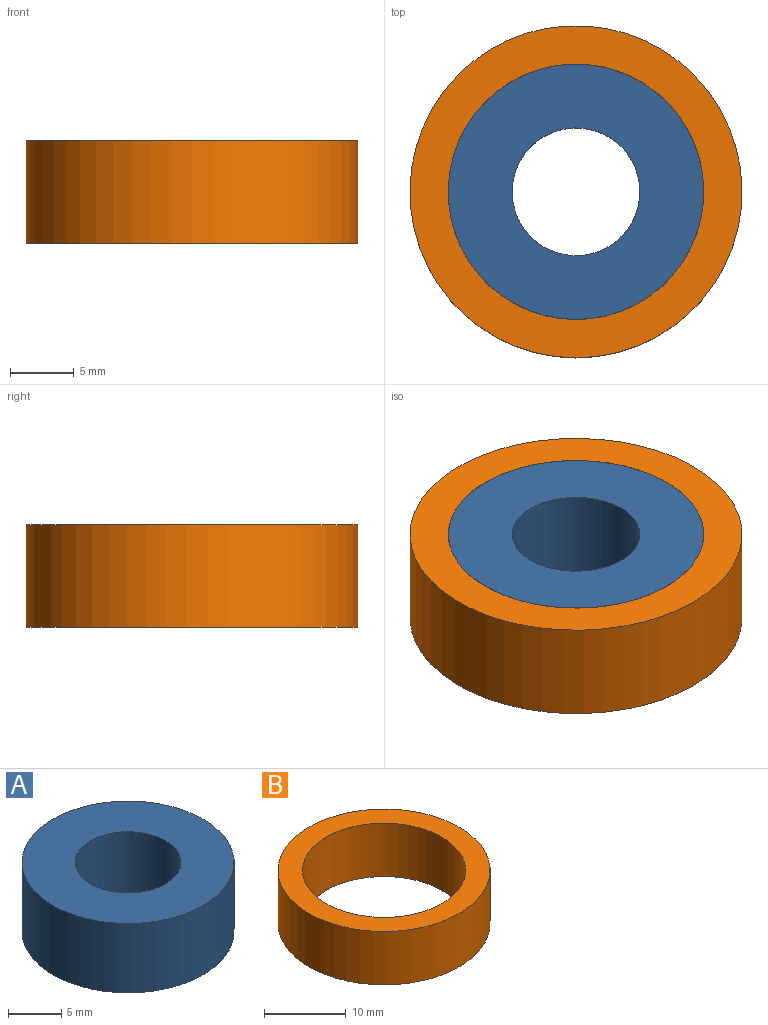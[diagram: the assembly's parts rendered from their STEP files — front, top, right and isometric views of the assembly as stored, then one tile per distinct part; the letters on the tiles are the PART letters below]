
ASSEMBLY  parts=2 mates=1
PART A: 4 faces, bbox 20x20x8 mm
  f0: cylinder r=5mm len=10mm, axis (0,0,-1), area 251.3mm2, adj f2,f3
  f1: cylinder r=10mm len=20mm, axis (0,0,-1), area 502.7mm2, adj f2,f3
  f2: plane 20x20mm, normal (0,0,1), area 235.6mm2, adj f0,f1
  f3: plane 20x20mm, normal (0,0,-1), area 235.6mm2, adj f0,f1
PART B: 4 faces, bbox 26x26x8 mm
  f0: cylinder r=10mm len=20mm, axis (0,0,-1), area 502.7mm2, adj f2,f3
  f1: cylinder r=13mm len=26mm, axis (0,0,-1), area 653.5mm2, adj f2,f3
  f2: plane 26x26mm, normal (0,0,1), area 216.8mm2, adj f0,f1
  f3: plane 26x26mm, normal (0,0,-1), area 216.8mm2, adj f0,f1
PLACE A t=(-3.08,-0.45,-0.5)mm
PLACE B rot(axis=(0,0,1),150deg) t=(-3.08,-0.45,-0.5)mm
MATE revolute B.f0 <-> A.f1  axis (0,0,-1) through (-3.08,-0.45,7.5)mm
